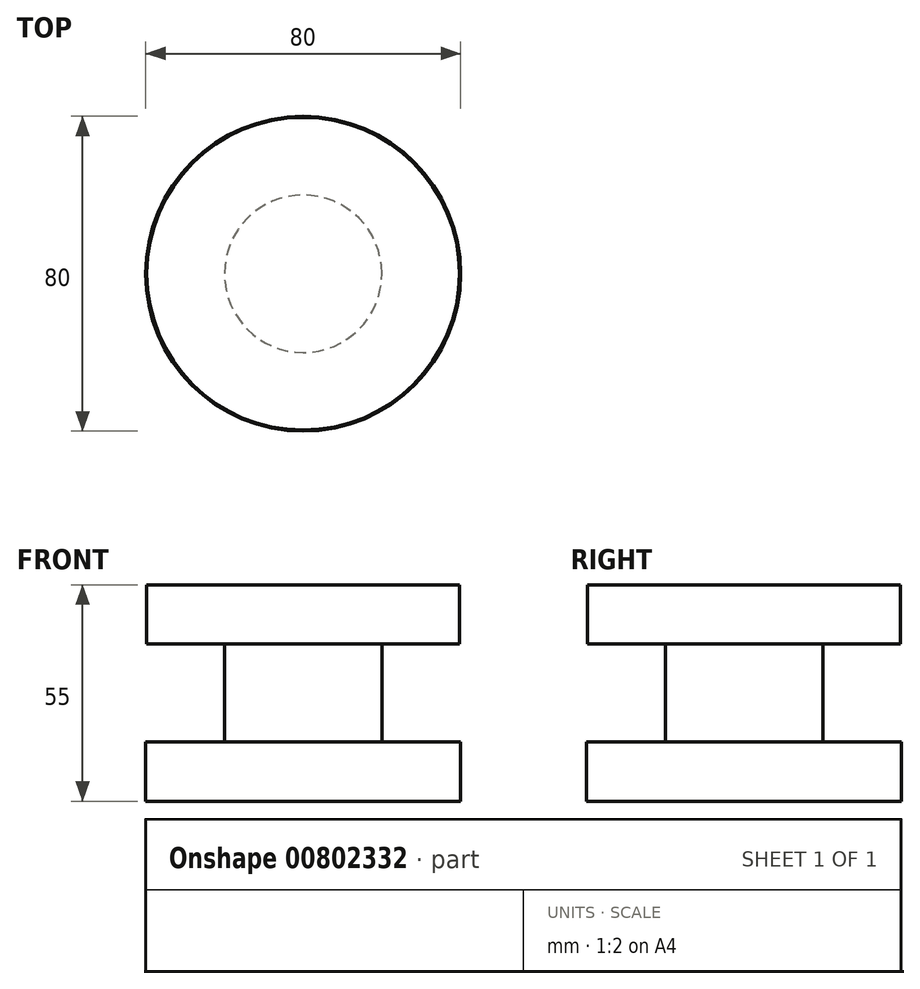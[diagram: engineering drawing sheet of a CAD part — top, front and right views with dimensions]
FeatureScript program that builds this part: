
annotation { "Feature Type Name" : "Feature", "Feature Type Description" : "" }
export const myFeature = defineFeature(function(context is Context, id is Id, definition is map)
    precondition{}
    {
        {
            var Q0;
            Q0=qCreatedBy(makeId("Top.planeOp"),FACE);
            var sketch = newSketch(context, id + "F0", { "sketchPlane" : qUnion([Q0])});
            skCircle(sketch, "E0", {"center": v(0, 0) * mm, "radius": 40 * mm});
            skSolve(sketch);
        }
        {
            var Q0;
            Q0 = qSketchRegion(id + "F0", true);
            extrude(context, id + "F1", {"entities" : qUnion([Q0]), "depth" : 15 * mm, "offsetDistance" : 25 * mm});
        }
        {
            var Q0;
            Q0=makeQuery(id+"F1.opExtrude","CAP_FACE",FACE,{"disambiguationData":[OSD([sQuery(id+"F0.wireOp",EDGE,"E0")])],"isStart":false});
            var sketch = newSketch(context, id + "F2", { "sketchPlane" : qUnion([Q0])});
            skCircle(sketch, "E1", {"center": v(0, 0) * mm, "radius": 20 * mm});
            skSolve(sketch);
        }
        {
            var Q0;
            Q0=makeQuery(id+"F2.imprint","IMPRINT",FACE,{"disambiguationData":[TD([[makeQuery(id+"F2.imprint","IMPRINT",EDGE,{"derivedFrom":sQuery(id+"F2.wireOp",EDGE,"E1")}),1.0]])]});
            extrude(context, id + "F3", {"entities" : qUnion([Q0]), "operationType" : NewBodyOperationType.ADD, "depth" : 25 * mm, "offsetDistance" : 25 * mm});
        }
        {
            var Q0;
            Q0=makeQuery(id+"F3.opExtrude","CAP_FACE",FACE,{"disambiguationData":[OSD([sQuery(id+"F2.wireOp",EDGE,"E1")])],"isStart":false});
            var sketch = newSketch(context, id + "F4", { "sketchPlane" : qUnion([Q0])});
            skCircle(sketch, "E2", {"center": v(0, 0) * mm, "radius": 39.71 * mm});
            skSolve(sketch);
        }
        {
            var Q0;
            Q0 = qSketchRegion(id + "F4", true);
            extrude(context, id + "F5", {"entities" : qUnion([Q0]), "operationType" : NewBodyOperationType.ADD, "depth" : 15 * mm, "offsetDistance" : 25 * mm});
        }
    });
